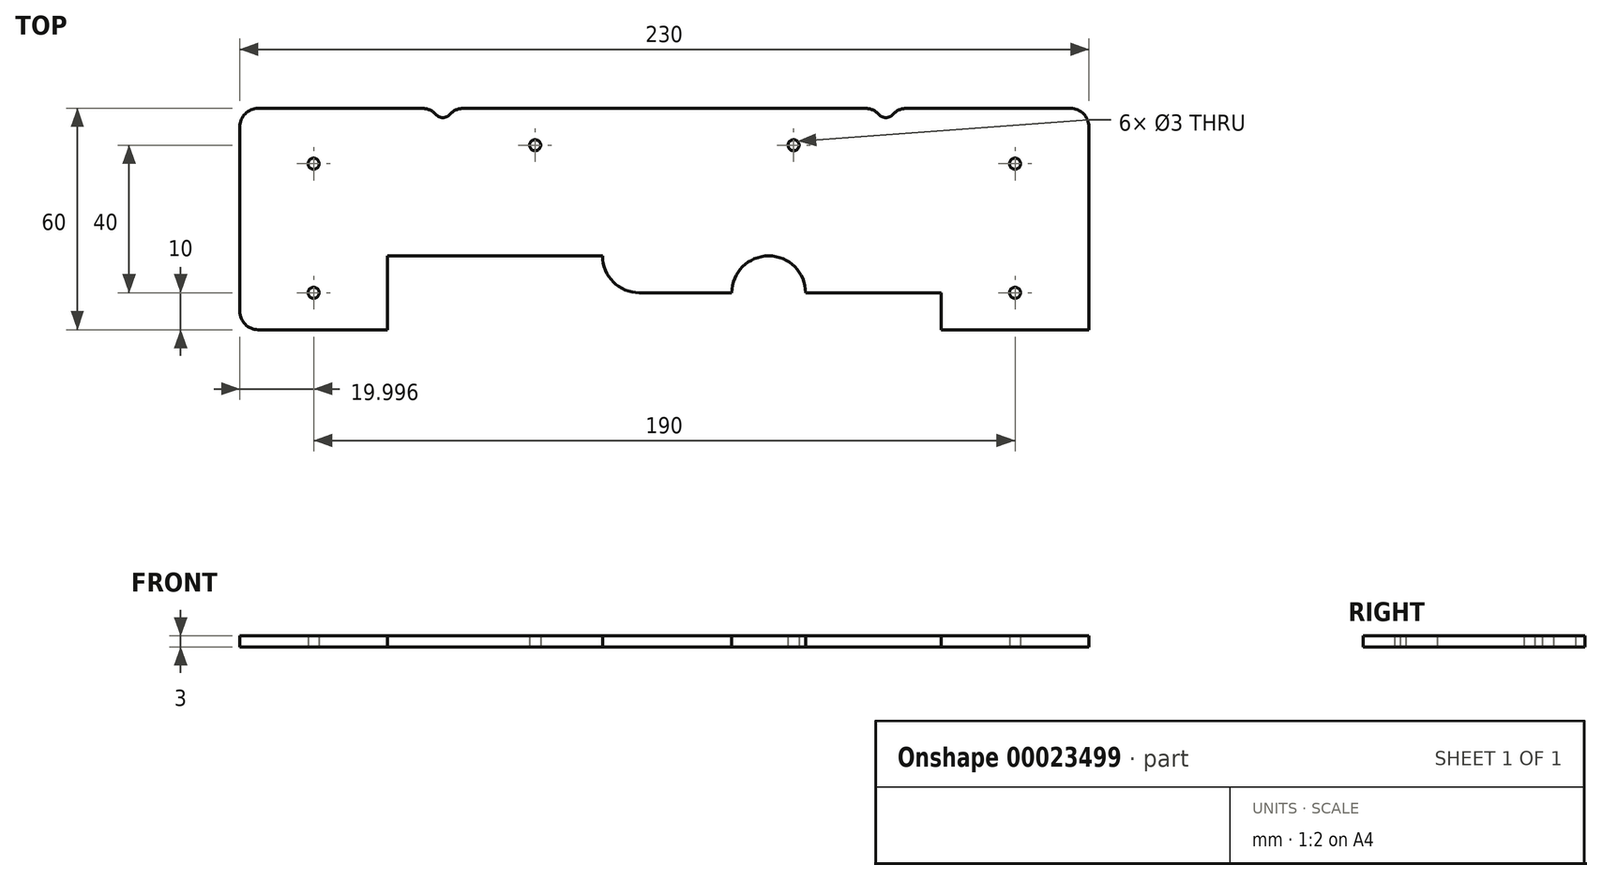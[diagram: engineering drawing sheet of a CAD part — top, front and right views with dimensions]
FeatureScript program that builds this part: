
annotation { "Feature Type Name" : "Feature", "Feature Type Description" : "" }
export const myFeature = defineFeature(function(context is Context, id is Id, definition is map)
    precondition{}
    {
        {
            var Q0;
            Q0=qCreatedBy(makeId("Top.planeOp"),FACE);
            var sketch = newSketch(context, id + "F0", { "sketchPlane" : qUnion([Q0])});
            skArc(sketch, "E0", {"start": v(10, 0) * mm, "mid": v(0, 10) * mm, "end": v(-10, 0) * mm});
            skArc(sketch, "E1", {"start": v(-45, 10) * mm, "mid": v(-42.07, 2.93) * mm, "end": v(-35, 0) * mm});
            skLineSegment(sketch, "E2.bottom", {"start": v(86.74, 50) * mm, "end": v(34.24, 50) * mm});
            skLineSegment(sketch, "E2.top", {"start": v(86.74, -10) * mm, "end": v(46.74, -10) * mm});
            skLineSegment(sketch, "E2.left", {"start": v(86.74, 50) * mm, "end": v(86.74, -10) * mm});
            skLineSegment(sketch, "E2.right", {"start": v(-143.26, 50) * mm, "end": v(-143.26, -10) * mm});
            skLineSegment(sketch, "E3", {"start": v(10, 0) * mm, "end": v(46.74, 0) * mm});
            skLineSegment(sketch, "E4", {"start": v(46.74, 0) * mm, "end": v(46.74, -10) * mm});
            skLineSegment(sketch, "E5", {"start": v(-10, 0) * mm, "end": v(-35, 0) * mm});
            skLineSegment(sketch, "E6", {"start": v(-45, 10) * mm, "end": v(-103.26, 10) * mm});
            skLineSegment(sketch, "E7", {"start": v(-103.26, 10) * mm, "end": v(-103.26, -10) * mm});
            skLineSegment(sketch, "E8.trimOffspring", {"start": v(-103.26, -10) * mm, "end": v(-143.26, -10) * mm});
            skPoint(sketch, "E9.start.orphan", {"position": v(0, 10) * mm});
            skCircle(sketch, "E10", {"center": v(-123.26, 0) * mm, "radius": 1.5 * mm});
            skCircle(sketch, "E11", {"center": v(-123.26, 35) * mm, "radius": 1.5 * mm});
            skCircle(sketch, "E12", {"center": v(66.74, 35) * mm, "radius": 1.5 * mm});
            skCircle(sketch, "E13", {"center": v(66.74, 0) * mm, "radius": 1.5 * mm});
            skCircle(sketch, "E14", {"center": v(-63.26, 40) * mm, "radius": 1.5 * mm});
            skCircle(sketch, "E15", {"center": v(6.74, 40) * mm, "radius": 1.5 * mm});
            skArc(sketch, "E16", {"start": v(-90.76, 50) * mm, "mid": v(-88.26, 47.5) * mm, "end": v(-85.76, 50) * mm});
            skArc(sketch, "E17", {"start": v(29.24, 50) * mm, "mid": v(31.74, 47.5) * mm, "end": v(34.24, 50) * mm});
            skLineSegment(sketch, "E18.trimOffspring", {"start": v(-90.76, 50) * mm, "end": v(-143.26, 50) * mm});
            skLineSegment(sketch, "E19.trimOffspring", {"start": v(29.24, 50) * mm, "end": v(-85.76, 50) * mm});
            skSolve(sketch);
        }
        {
            var Q0;
            Q0 = qSketchRegion(id + "F0", true);
            extrude(context, id + "F1", {"entities" : qUnion([Q0]), "depth" : 3 * mm});
        }
        {
            var Q0;
            Q0=makeQuery(id+"F1.opExtrude","SWEPT_EDGE",EDGE,{"disambiguationData":[OSD([sQuery(id+"F0.wireOp",EDGE,"E2.bottom"),sQuery(id+"F0.wireOp",EDGE,"E2.right")])]});
            var Q1;
            Q1=makeQuery(id+"F1.opExtrude","SWEPT_EDGE",EDGE,{"disambiguationData":[OSD([sQuery(id+"F0.wireOp",EDGE,"E2.bottom"),sQuery(id+"F0.wireOp",EDGE,"E2.left")])]});
            fillet(context, id + "F2", {"entities" : qUnion([Q0, Q1]), "radius" : 5 * mm, "tangentPropagation" : true, "allowEdgeOverflow" : false});
        }
        {
            var Q0;
            Q0=makeQuery(id+"F1.opExtrude","SWEPT_EDGE",EDGE,{"disambiguationData":[OSD([sQuery(id+"F0.wireOp",EDGE,"E16"),sQuery(id+"F0.wireOp",EDGE,"E18.trimOffspring")])]});
            var Q1;
            Q1=makeQuery(id+"F1.opExtrude","SWEPT_EDGE",EDGE,{"disambiguationData":[OSD([sQuery(id+"F0.wireOp",EDGE,"E16"),sQuery(id+"F0.wireOp",EDGE,"E19.trimOffspring")])]});
            var Q2;
            Q2=makeQuery(id+"F1.opExtrude","SWEPT_EDGE",EDGE,{"disambiguationData":[OSD([sQuery(id+"F0.wireOp",EDGE,"E17"),sQuery(id+"F0.wireOp",EDGE,"E19.trimOffspring")])]});
            fillet(context, id + "F3", {"entities" : qUnion([Q0, Q1, Q2]), "radius" : 5 * mm, "tangentPropagation" : true, "allowEdgeOverflow" : false});
        }
    });
